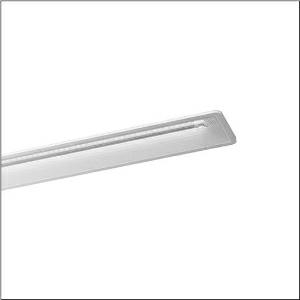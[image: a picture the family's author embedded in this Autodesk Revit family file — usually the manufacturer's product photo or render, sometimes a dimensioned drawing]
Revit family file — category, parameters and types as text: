
# Revit family: taris_r__21_5mt115d03wd_575d
name_source: partatom
category: Lighting Fixtures
units: mm (PartAtom-declared; Revit-internal decimal feet)

## family parameters
Cut with Voids When Loaded = No
Host = Face
Light Source = No
Part Type = Normal
Room Calculation Point = No
Round Connector Dimension = Use Diameter
Shared = No

## types (1)
- --- (1 x LED, 3420 lm, 22.2 W, 3000K)
    Apparent Load = 22 VA
    CIE Flux Codes = 73 96 99 100 100
    Color Rendering = 80
    Color Temperature = 3000K
    Default Elevation = 1800 mm
    Description = Taris® 21, office luminaire, primary anti-glare with micro louvre, primary optical cover: axial lens, of PMMA, structured, CAT 2 (L<= 1500cd/m²), light emission: direct distribution, primary light characteristic: symmetric, installation type: recessed, LED rated luminous flux: 3.420 lm, light colour: 830, colour temperature: 3000K, control gear: ECG DALI, with terminal, 5-pole, mains connection: 230V, AC, 50Hz, rated input power: 22W, housing, luminaire housing, of plastic, traffic white (RAL 9016), length: 968 mm, width: 150 mm, height: 76mm, recess depth: 106 mm, protection rating (complete): IP20, insulation class (complete): insulation class I (protective earthing), certification: CE, ENEC, VDE, protection symbol: F, impact resistance: IK02, permissible ambient temperature for indoor applications: 0..+35°C, standard: EN 50419, packaging unit: 1 piece
    Height = 0 mm  [stored 0 ft]
    Lamp = 1 x LED
    Lamp Light Flux = 3420 lm
    Lamp Power = 22.2 W
    Lamp count = 1
    Length = 962 mm
    Luminous efficacy = 154 lm/W
    Manufacturer = Siteco
    ModVariant = No
    Model = 5MT115D03WD
    Mounting Place = Ceiling
    Mounting Type = Recessed
    Number of Poles = 1
    OnlyDefault = Yes
    Power Factor = 1
    Product Name = Taris® 21
    Product group = office luminaire | ceiling recessed
    ProductGroupID = 400
    Protection Class = Protection class I
    Protection Degree = IP 20
    RLX_Detail_Level = 1
    RlxData = <blob elided: 29569 chars, md5=ef842bfc>
    Socket = socket
    Standby Power = 0 W
    System Light Flux = 3420 lm
    System Power = 22 W
    Type Comments = factory setting: luminous flux: 100 % | dim-lin: 254 | 200 mA
    Type Image = l_1004723.jpg
    URL = http://relux.com
    VarID = @adj_130277
    Voltage = 0 V
    Weight = 0.00 kg
    Width = 144 mm

note: [stored X ft] marks values corroborated as IEEE doubles in the binary element streams (Revit-internal decimal feet)

## geometry (parser evidence)
native form markers: Blend x4, Sweep x11
no freeform markers — native parametric forms only
